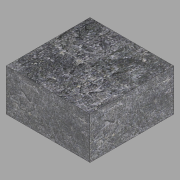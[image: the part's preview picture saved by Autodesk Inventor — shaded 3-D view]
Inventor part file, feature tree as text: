
AUTODESK INVENTOR PART (.ipt)
format: ipt  version: 2022.2 (Build 262287000, 287)  size: 125,440 bytes
history: native  units: in
note: dims shown in document units (in); Inventor stores cm internally (conversion verified against a paired STEP export)
features: extrude x1, sketch x1
ambient origin geometry x8: Origin, YZ Plane, XZ Plane, XY Plane, X Axis, Y Axis, Z Axis, Center Point
bodies: Solid1 (feature_tree)
feature tree (2):
  extrude  "Extrusion1"  Depth=4.0in
  sketch  "Sketch1"  dims[d0=4.0in d1=4.0in d2=2.0in d3=0.0in]
